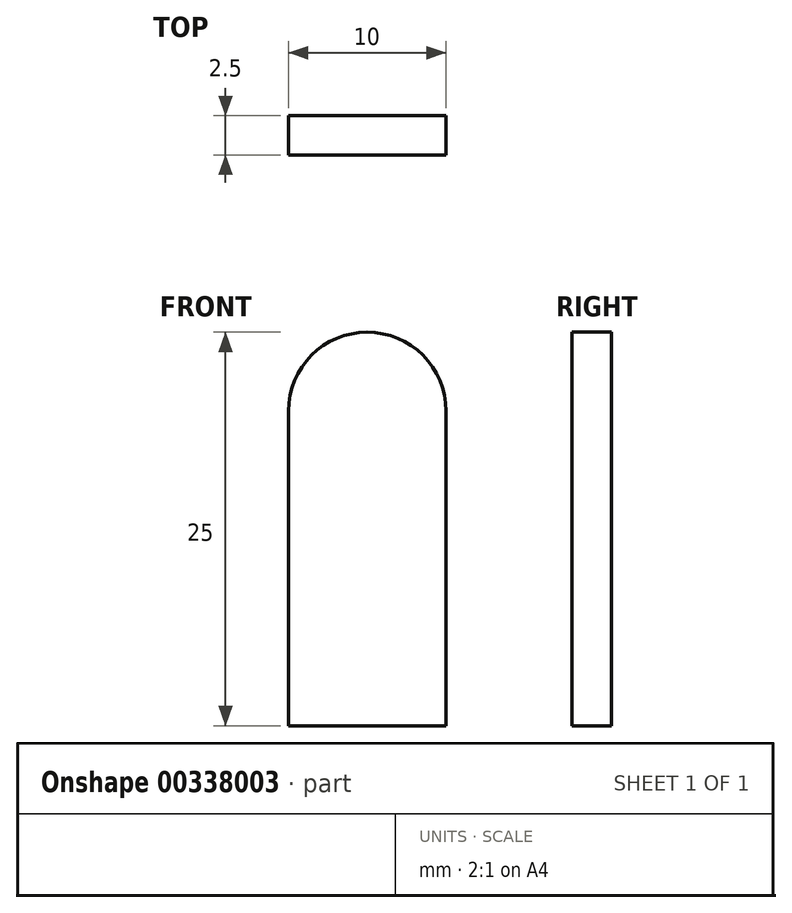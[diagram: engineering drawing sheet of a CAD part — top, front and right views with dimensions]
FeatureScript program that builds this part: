
annotation { "Feature Type Name" : "Feature", "Feature Type Description" : "" }
export const myFeature = defineFeature(function(context is Context, id is Id, definition is map)
    precondition{}
    {
        {
            var Q0;
            Q0=qCreatedBy(makeId("Front.planeOp"),FACE);
            var sketch = newSketch(context, id + "F0", { "sketchPlane" : qUnion([Q0])});
            skCircle(sketch, "E0", {"center": v(0, 0) * mm, "radius": 27.5 * mm, "construction": true});
            skLineSegment(sketch, "E1", {"start": v(-27.5, 0) * mm, "end": v(-27.5, -36) * mm, "construction": true});
            skLineSegment(sketch, "E2", {"start": v(27.5, -36) * mm, "end": v(27.5, 0) * mm, "construction": true});
            skCircle(sketch, "E3", {"center": v(0, 0) * mm, "radius": 27.5 * mm});
            skLineSegment(sketch, "E4", {"start": v(-27.5, -36) * mm, "end": v(-27.5, 0) * mm});
            skLineSegment(sketch, "E5", {"start": v(27.5, -36) * mm, "end": v(27.5, 0) * mm});
            skLineSegment(sketch, "E6", {"start": v(-27.5, -36) * mm, "end": v(27.5, -36) * mm});
            skSolve(sketch);
        }
        {
            var Q0;
            {var subQ0=sQuery(id+"F0.wireOp",EDGE,"E3");var subQ1=makeQuery(id+"F0.imprint","INTERSECT",VERTEX,{"derivedFrom":[subQ0,sQuery(id+"F0.wireOp",EDGE,"E4")]});Q0=makeQuery(id+"F0.imprint","IMPRINT",FACE,{"disambiguationData":[TD([[makeQuery(id+"F0.imprint","IMPRINT",EDGE,{"disambiguationData":[TD([[subQ1,1.0]])],"derivedFrom":subQ0}),1.0]])]});}
            var Q1;
            {var subQ0=sQuery(id+"F0.wireOp",EDGE,"E4");Q1=makeQuery(id+"F0.imprint","IMPRINT",FACE,{"disambiguationData":[TD([[makeQuery(id+"F0.imprint","IMPRINT",EDGE,{"derivedFrom":subQ0}),-1.0]])]});}
            extrude(context, id + "F1", {"entities" : qUnion([Q0, Q1]), "oppositeDirection" : true, "depth" : 90 * mm});
        }
        {
            var Q0;
            Q0=makeQuery(id+"F1.opExtrude","CAP_FACE",FACE,{"disambiguationData":[OSD([sQuery(id+"F0.wireOp",EDGE,"E3"),sQuery(id+"F0.wireOp",EDGE,"E4"),sQuery(id+"F0.wireOp",EDGE,"E5"),sQuery(id+"F0.wireOp",EDGE,"E6")])],"isStart":true});
            var Q1;
            Q1=makeQuery(id+"F1.opExtrude","SWEPT_FACE",FACE,{"disambiguationData":[OSD([sQuery(id+"F0.wireOp",EDGE,"E6")])]});
            shell(context, id + "F2", {"entities" : qUnion([Q0, Q1]), "thickness" : 2.5 * mm});
        }
        {
            var Q0;
            Q0=makeQuery(id+"F1.opExtrude","CAP_FACE",FACE,{"disambiguationData":[OSD([sQuery(id+"F0.wireOp",EDGE,"E3"),sQuery(id+"F0.wireOp",EDGE,"E4"),sQuery(id+"F0.wireOp",EDGE,"E5"),sQuery(id+"F0.wireOp",EDGE,"E6")])],"isStart":false});
            var sketch = newSketch(context, id + "F3", { "sketchPlane" : qUnion([Q0])});
            skLineSegment(sketch, "E7.bottom", {"start": v(5, -16) * mm, "end": v(-5, -16) * mm, "construction": true});
            skLineSegment(sketch, "E7.top", {"start": v(5, -56) * mm, "end": v(-5, -56) * mm, "construction": true});
            skLineSegment(sketch, "E7.left", {"start": v(5, -16) * mm, "end": v(5, -56) * mm, "construction": true});
            skLineSegment(sketch, "E7.right", {"start": v(-5, -16) * mm, "end": v(-5, -56) * mm, "construction": true});
            skPoint(sketch, "E7.middle", {"position": v(0, -36) * mm});
            skLineSegment(sketch, "E8", {"start": v(0, -36) * mm, "end": v(0, 0) * mm, "construction": true});
            skPoint(sketch, "E9", {"position": v(0, -16) * mm});
            skArc(sketch, "E10", {"start": v(-5, -16) * mm, "mid": v(0, -11) * mm, "end": v(5, -16) * mm});
            skLineSegment(sketch, "E11", {"start": v(-5, -16) * mm, "end": v(-5, -36) * mm});
            skLineSegment(sketch, "E12", {"start": v(-5, -36) * mm, "end": v(5, -36) * mm});
            skLineSegment(sketch, "E13", {"start": v(5, -36) * mm, "end": v(5, -16) * mm});
            skSolve(sketch);
        }
        {
            var Q0;
            Q0=makeQuery(id+"F3.imprint","IMPRINT",FACE,{"disambiguationData":[TD([[makeQuery(id+"F3.imprint","IMPRINT",EDGE,{"derivedFrom":sQuery(id+"F3.wireOp",EDGE,"E10")}),-1.0]])]});
            extrude(context, id + "F4", {"entities" : qUnion([Q0]), "operationType" : NewBodyOperationType.REMOVE, "endBound" : BoundingType.THROUGH_ALL, "oppositeDirection" : true, "depth" : 25 * mm});
        }
    });
